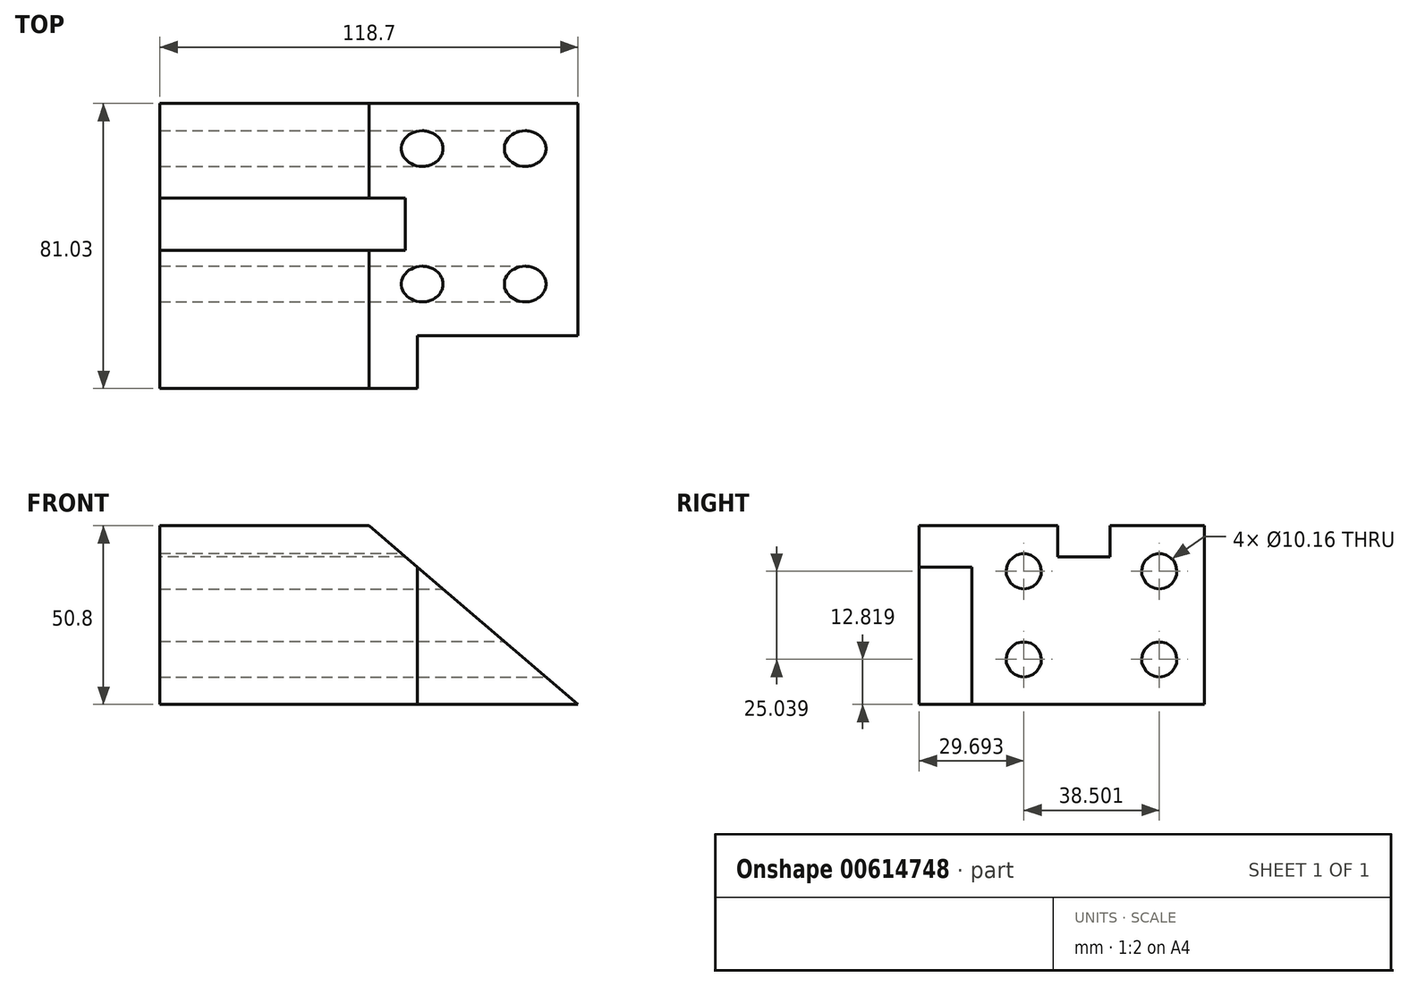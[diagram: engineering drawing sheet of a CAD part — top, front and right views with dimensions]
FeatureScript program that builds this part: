
annotation { "Feature Type Name" : "Feature", "Feature Type Description" : "" }
export const myFeature = defineFeature(function(context is Context, id is Id, definition is map)
    precondition{}
    {
        {
            var Q0;
            Q0=qCreatedBy(makeId("Top.planeOp"),FACE);
            var sketch = newSketch(context, id + "F0", { "sketchPlane" : qUnion([Q0])});
            skLineSegment(sketch, "E0.bottom", {"start": v(59.35, -34.29) * mm, "end": v(-59.35, -34.29) * mm});
            skLineSegment(sketch, "E0.top", {"start": v(59.35, 34.29) * mm, "end": v(-59.35, 34.29) * mm});
            skLineSegment(sketch, "E0.left", {"start": v(59.35, -34.29) * mm, "end": v(59.35, 34.29) * mm});
            skLineSegment(sketch, "E0.right", {"start": v(-59.35, -34.29) * mm, "end": v(-59.35, 34.29) * mm});
            skPoint(sketch, "E0.middle", {"position": v(0, 0) * mm});
            skSolve(sketch);
        }
        {
            var Q0;
            Q0=makeQuery(id+"F0.imprint","IMPRINT",FACE,{"disambiguationData":[TD([[makeQuery(id+"F0.imprint","IMPRINT",EDGE,{"derivedFrom":sQuery(id+"F0.wireOp",EDGE,"E0.bottom")}),-1.0]])]});
            extrude(context, id + "F1", {"entities" : qUnion([Q0]), "depth" : 50.8 * mm, "offsetDistance" : 25.4 * mm});
        }
        {
            var Q0;
            Q0=makeQuery(id+"F1.opExtrude","SWEPT_FACE",FACE,{"disambiguationData":[OSD([sQuery(id+"F0.wireOp",EDGE,"E0.left")])]});
            var sketch = newSketch(context, id + "F2", { "sketchPlane" : qUnion([Q0])});
            skCircle(sketch, "E1", {"center": v(-17.05, 37.86) * mm, "radius": 5.08 * mm});
            skCircle(sketch, "E2", {"center": v(-17.05, 12.82) * mm, "radius": 5.08 * mm});
            skCircle(sketch, "E3", {"center": v(21.45, 12.82) * mm, "radius": 5.08 * mm});
            skCircle(sketch, "E4", {"center": v(21.45, 37.86) * mm, "radius": 5.08 * mm});
            skSolve(sketch);
        }
        {
            var Q0;
            Q0=makeQuery(id+"F2.imprint","IMPRINT",FACE,{"disambiguationData":[TD([[makeQuery(id+"F2.imprint","IMPRINT",EDGE,{"derivedFrom":sQuery(id+"F2.wireOp",EDGE,"E2")}),1.0]])]});
            var Q1;
            Q1=makeQuery(id+"F2.imprint","IMPRINT",FACE,{"disambiguationData":[TD([[makeQuery(id+"F2.imprint","IMPRINT",EDGE,{"derivedFrom":sQuery(id+"F2.wireOp",EDGE,"E3")}),1.0]])]});
            var Q2;
            Q2=makeQuery(id+"F2.imprint","IMPRINT",FACE,{"disambiguationData":[TD([[makeQuery(id+"F2.imprint","IMPRINT",EDGE,{"derivedFrom":sQuery(id+"F2.wireOp",EDGE,"E4")}),1.0]])]});
            var Q3;
            Q3=makeQuery(id+"F2.imprint","IMPRINT",FACE,{"disambiguationData":[TD([[makeQuery(id+"F2.imprint","IMPRINT",EDGE,{"derivedFrom":sQuery(id+"F2.wireOp",EDGE,"E1")}),1.0]])]});
            extrude(context, id + "F3", {"entities" : qUnion([Q0, Q1, Q2, Q3]), "operationType" : NewBodyOperationType.REMOVE, "oppositeDirection" : true, "depth" : 101.6 * mm, "offsetDistance" : 25.4 * mm});
        }
        {
            var Q0;
            Q0=makeQuery(id+"F1.opExtrude","SWEPT_FACE",FACE,{"disambiguationData":[OSD([sQuery(id+"F0.wireOp",EDGE,"E0.bottom")])]});
            extrude(context, id + "F4", {"entities" : qUnion([Q0]), "operationType" : NewBodyOperationType.ADD, "depth" : 12.45 * mm, "offsetDistance" : 25.4 * mm});
        }
        {
            var Q0;
            Q0=makeQuery(id+"F3.boolean.opBoolean","COPY",FACE,{"derivedFrom":makeQuery(id+"F3.opExtrude","CAP_FACE",FACE,{"disambiguationData":[OSD([sQuery(id+"F2.wireOp",EDGE,"E1")])],"isStart":false})});
            var Q1;
            Q1=makeQuery(id+"F3.boolean.opBoolean","COPY",FACE,{"derivedFrom":makeQuery(id+"F3.opExtrude","CAP_FACE",FACE,{"disambiguationData":[OSD([sQuery(id+"F2.wireOp",EDGE,"E3")])],"isStart":false})});
            var Q2;
            Q2=makeQuery(id+"F3.boolean.opBoolean","COPY",FACE,{"derivedFrom":makeQuery(id+"F3.opExtrude","CAP_FACE",FACE,{"disambiguationData":[OSD([sQuery(id+"F2.wireOp",EDGE,"E2")])],"isStart":false})});
            var Q3;
            Q3=makeQuery(id+"F3.boolean.opBoolean","COPY",FACE,{"derivedFrom":makeQuery(id+"F3.opExtrude","CAP_FACE",FACE,{"disambiguationData":[OSD([sQuery(id+"F2.wireOp",EDGE,"E4")])],"isStart":false})});
            extrude(context, id + "F5", {"entities" : qUnion([Q0, Q1, Q2, Q3]), "operationType" : NewBodyOperationType.REMOVE, "oppositeDirection" : true, "depth" : 82.04 * mm, "offsetDistance" : 25.4 * mm});
        }
        {
            var Q0;
            Q0=makeQuery(id+"F4.opExtrude","CAP_FACE",FACE,{"disambiguationData":[OSD([sQuery(id+"F0.wireOp",EDGE,"E0.bottom")])],"isStart":false});
            var sketch = newSketch(context, id + "F6", { "sketchPlane" : qUnion([Q0])});
            skLineSegment(sketch, "E5", {"start": v(0, 50.8) * mm, "end": v(59.35, 0) * mm});
            skLineSegment(sketch, "E6", {"start": v(59.35, 0) * mm, "end": v(59.35, 50.8) * mm});
            skLineSegment(sketch, "E7", {"start": v(59.35, 50.8) * mm, "end": v(0, 50.8) * mm});
            skSolve(sketch);
        }
        {
            var Q0;
            Q0=makeQuery(id+"F6.imprint","IMPRINT",FACE,{"disambiguationData":[TD([[makeQuery(id+"F6.imprint","IMPRINT",EDGE,{"derivedFrom":sQuery(id+"F6.wireOp",EDGE,"E5")}),1.0]])]});
            extrude(context, id + "F7", {"entities" : qUnion([Q0]), "operationType" : NewBodyOperationType.REMOVE, "oppositeDirection" : true, "depth" : 187.96 * mm, "offsetDistance" : 25.4 * mm});
        }
        {
            var Q0;
            Q0=makeQuery(id+"F4.opExtrude","CAP_FACE",FACE,{"disambiguationData":[OSD([sQuery(id+"F0.wireOp",EDGE,"E0.bottom")])],"isStart":false});
            var sketch = newSketch(context, id + "F8", { "sketchPlane" : qUnion([Q0])});
            skLineSegment(sketch, "E8", {"start": v(13.76, 39.02) * mm, "end": v(13.76, 0) * mm});
            skLineSegment(sketch, "E9", {"start": v(13.76, 0) * mm, "end": v(59.35, 0) * mm});
            skLineSegment(sketch, "E10", {"start": v(59.35, 0) * mm, "end": v(13.76, 39.02) * mm});
            skLineSegment(sketch, "E11", {"start": v(-96.83, 81.73) * mm, "end": v(-109.43, 74.25) * mm});
            skSolve(sketch);
        }
        {
            var Q0;
            Q0=makeQuery(id+"F8.imprint","IMPRINT",FACE,{"disambiguationData":[TD([[makeQuery(id+"F8.imprint","IMPRINT",EDGE,{"derivedFrom":sQuery(id+"F8.wireOp",EDGE,"E8")}),1.0]])]});
            extrude(context, id + "F9", {"entities" : qUnion([Q0]), "operationType" : NewBodyOperationType.REMOVE, "oppositeDirection" : true, "depth" : 15 * mm, "offsetDistance" : 25.4 * mm});
        }
        {
            var Q0;
            {var subQ0=sQuery(id+"F0.wireOp",EDGE,"E0.right");Q0=makeQuery(id+"F4.boolean.opBoolean","MERGE",FACE,{"derivedFrom":[makeQuery(id+"F1.opExtrude","SWEPT_FACE",FACE,{"disambiguationData":[OSD([subQ0])]}),makeQuery(id+"F4.opExtrude","SWEPT_FACE",FACE,{"disambiguationData":[OSD([sQuery(id+"F0.wireOp",EDGE,"E0.bottom"),subQ0])]})]});}
            var sketch = newSketch(context, id + "F10", { "sketchPlane" : qUnion([Q0])});
            skLineSegment(sketch, "E12.bottom", {"start": v(7.4, 41.96) * mm, "end": v(-7.4, 41.96) * mm});
            skLineSegment(sketch, "E12.top", {"start": v(7.4, 59.64) * mm, "end": v(-7.4, 59.64) * mm});
            skLineSegment(sketch, "E12.left", {"start": v(7.4, 41.96) * mm, "end": v(7.4, 59.64) * mm});
            skLineSegment(sketch, "E12.right", {"start": v(-7.4, 41.96) * mm, "end": v(-7.4, 59.64) * mm});
            skPoint(sketch, "E12.middle", {"position": v(0, 50.8) * mm});
            skSolve(sketch);
        }
        {
            var Q0;
            {var subQ0=sQuery(id+"F10.wireOp",EDGE,"E12.bottom");Q0=makeQuery(id+"F10.imprint","IMPRINT",FACE,{"disambiguationData":[TD([[makeQuery(id+"F10.imprint","IMPRINT",EDGE,{"derivedFrom":subQ0}),-1.0]])]});}
            var Q1;
            {var subQ0=sQuery(id+"F10.wireOp",EDGE,"E12.top");Q1=makeQuery(id+"F10.imprint","IMPRINT",FACE,{"disambiguationData":[TD([[makeQuery(id+"F10.imprint","IMPRINT",EDGE,{"derivedFrom":subQ0}),1.0]])]});}
            extrude(context, id + "F11", {"entities" : qUnion([Q0, Q1]), "operationType" : NewBodyOperationType.REMOVE, "oppositeDirection" : true, "depth" : 191.26 * mm, "offsetDistance" : 25.4 * mm});
        }
    });
